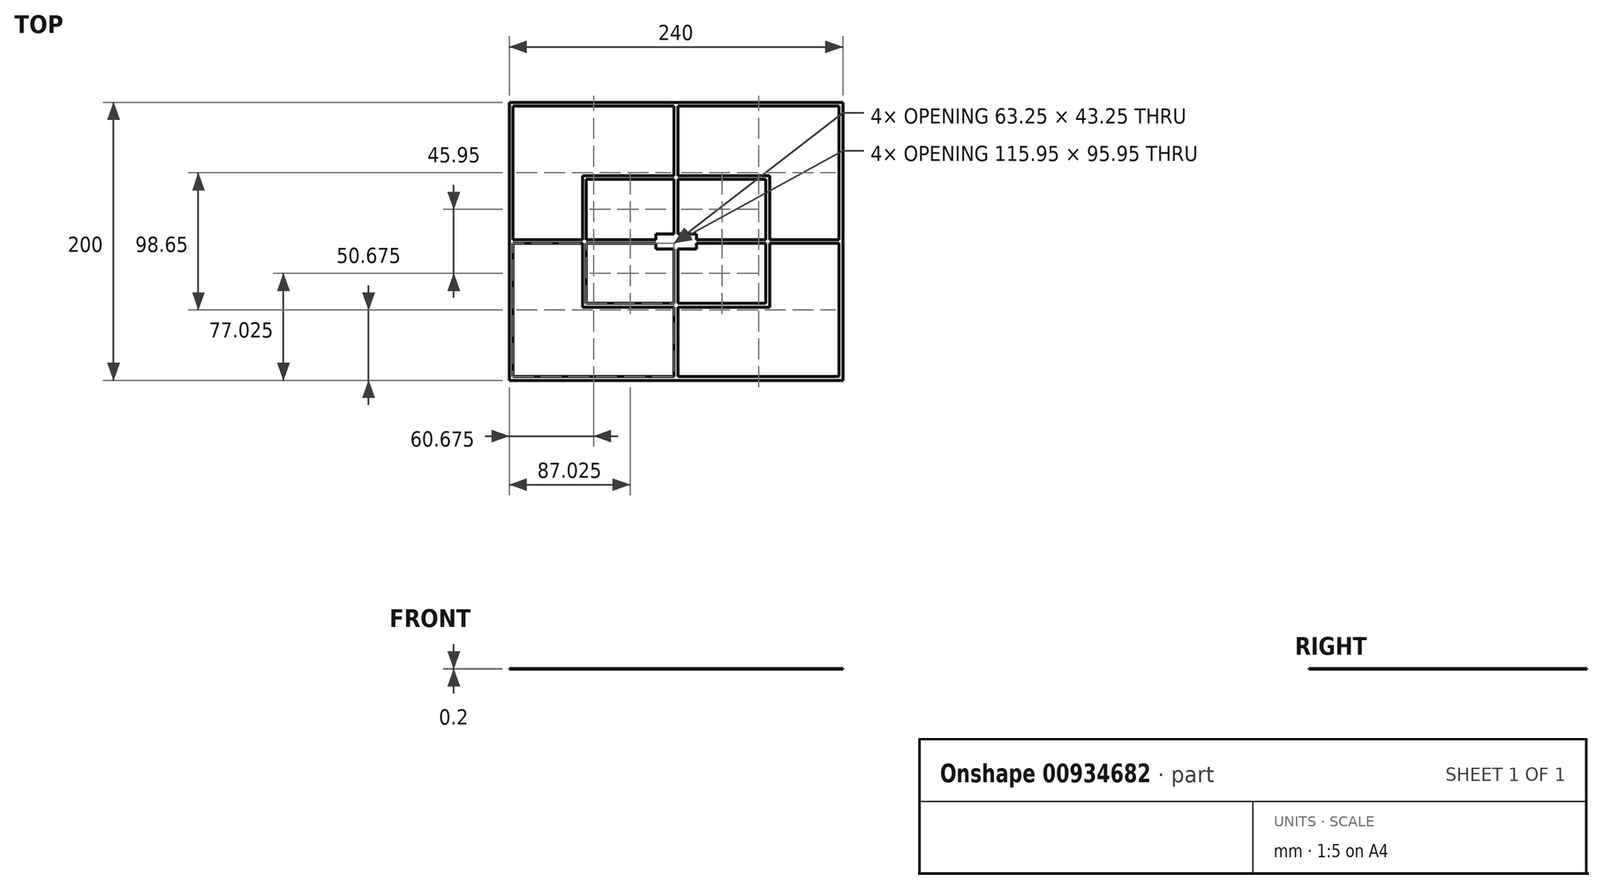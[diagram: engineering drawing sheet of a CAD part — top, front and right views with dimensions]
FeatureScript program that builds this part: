
annotation { "Feature Type Name" : "Feature", "Feature Type Description" : "" }
export const myFeature = defineFeature(function(context is Context, id is Id, definition is map)
    precondition{}
    {
        {
            assignVariable(context, id + "F0", {"variableType" : VariableType.LENGTH, "name" : "t", "lengthValue" : 0.2 * mm});
        }
        {
            var Q0;
            Q0=qCreatedBy(makeId("Top.planeOp"),FACE);
            var sketch = newSketch(context, id + "F1", { "sketchPlane" : qUnion([Q0])});
            skLineSegment(sketch, "E0.bottom", {"start": v(120, -100) * mm, "end": v(-120, -100) * mm});
            skLineSegment(sketch, "E0.top", {"start": v(120, 100) * mm, "end": v(-120, 100) * mm});
            skLineSegment(sketch, "E0.left", {"start": v(120, -100) * mm, "end": v(120, 100) * mm});
            skLineSegment(sketch, "E0.right", {"start": v(-120, -100) * mm, "end": v(-120, 100) * mm});
            skPoint(sketch, "E0.middle", {"position": v(0, 0) * mm});
            skLineSegment(sketch, "E1.0", {"start": v(117.3, -97.3) * mm, "end": v(117.3, -1.35) * mm});
            skLineSegment(sketch, "E1.1", {"start": v(117.3, -97.3) * mm, "end": v(1.35, -97.3) * mm});
            skLineSegment(sketch, "E1.2", {"start": v(-117.3, -97.3) * mm, "end": v(-117.3, -1.35) * mm});
            skLineSegment(sketch, "E1.3", {"start": v(117.3, 97.3) * mm, "end": v(1.35, 97.3) * mm});
            skLineSegment(sketch, "E2.0", {"start": v(-67.3, -47.3) * mm, "end": v(-67.3, -1.35) * mm});
            skLineSegment(sketch, "E2.1", {"start": v(67.3, -47.3) * mm, "end": v(1.35, -47.3) * mm});
            skLineSegment(sketch, "E2.2", {"start": v(67.3, -47.3) * mm, "end": v(67.3, -1.35) * mm});
            skLineSegment(sketch, "E2.3", {"start": v(67.3, 47.3) * mm, "end": v(1.35, 47.3) * mm});
            skLineSegment(sketch, "E3.0", {"start": v(64.6, -44.6) * mm, "end": v(1.35, -44.6) * mm});
            skLineSegment(sketch, "E3.1", {"start": v(64.6, -44.6) * mm, "end": v(64.6, -1.35) * mm});
            skLineSegment(sketch, "E3.2", {"start": v(64.6, 44.6) * mm, "end": v(1.35, 44.6) * mm});
            skLineSegment(sketch, "E3.3", {"start": v(-64.6, -44.6) * mm, "end": v(-64.6, -1.35) * mm});
            skLineSegment(sketch, "E4.0", {"start": v(14.6, 5.4) * mm, "end": v(1.35, 5.4) * mm});
            skLineSegment(sketch, "E4.1", {"start": v(14.6, 1.35) * mm, "end": v(14.6, 5.4) * mm});
            skLineSegment(sketch, "E4.2", {"start": v(14.6, -5.4) * mm, "end": v(1.35, -5.4) * mm});
            skLineSegment(sketch, "E4.3", {"start": v(-14.6, 1.35) * mm, "end": v(-14.6, 5.4) * mm});
            skLineSegment(sketch, "E5", {"start": v(14.6, -1.35) * mm, "end": v(64.6, -1.35) * mm});
            skLineSegment(sketch, "E6", {"start": v(67.3, -1.35) * mm, "end": v(117.3, -1.35) * mm});
            skLineSegment(sketch, "E7.MirrorCS", {"start": v(14.6, 1.35) * mm, "end": v(64.6, 1.35) * mm});
            skLineSegment(sketch, "E8.MirrorCS", {"start": v(67.3, 1.35) * mm, "end": v(117.3, 1.35) * mm});
            skPoint(sketch, "E9.orphan", {"position": v(64.6, 1.35) * mm});
            skLineSegment(sketch, "E10.trimOffspring", {"start": v(67.3, 1.35) * mm, "end": v(67.3, 47.3) * mm});
            skLineSegment(sketch, "E11.trimOffspring", {"start": v(64.6, 1.35) * mm, "end": v(64.6, 44.6) * mm});
            skLineSegment(sketch, "E12.trimOffspring", {"start": v(117.3, 1.35) * mm, "end": v(117.3, 97.3) * mm});
            skLineSegment(sketch, "E13.trimOffspring", {"start": v(14.6, -5.4) * mm, "end": v(14.6, -1.35) * mm});
            skLineSegment(sketch, "E14", {"start": v(1.35, 5.4) * mm, "end": v(1.35, 44.6) * mm});
            skLineSegment(sketch, "E15.MirrorCS", {"start": v(-1.35, 5.4) * mm, "end": v(-1.35, 44.6) * mm});
            skLineSegment(sketch, "E16.trimOffspring", {"start": v(-1.35, 97.3) * mm, "end": v(-117.3, 97.3) * mm});
            skPoint(sketch, "E17.orphan", {"position": v(1.35, 100) * mm});
            skPoint(sketch, "E18.orphan", {"position": v(-1.35, 100) * mm});
            skLineSegment(sketch, "E19.trimOffspring", {"start": v(-1.35, 44.6) * mm, "end": v(-64.6, 44.6) * mm});
            skLineSegment(sketch, "E20.trimOffspring", {"start": v(-1.35, 47.3) * mm, "end": v(-67.3, 47.3) * mm});
            skLineSegment(sketch, "E21.trimOffspring", {"start": v(-1.35, 47.3) * mm, "end": v(-1.35, 97.3) * mm});
            skLineSegment(sketch, "E22.trimOffspring", {"start": v(1.35, 47.3) * mm, "end": v(1.35, 97.3) * mm});
            skLineSegment(sketch, "E23.trimOffspring", {"start": v(-1.35, 5.4) * mm, "end": v(-14.6, 5.4) * mm});
            skLineSegment(sketch, "E24.MirrorCS", {"start": v(1.35, -5.4) * mm, "end": v(1.35, -44.6) * mm});
            skLineSegment(sketch, "E25.MirrorCS", {"start": v(-1.35, -5.4) * mm, "end": v(-1.35, -44.6) * mm});
            skLineSegment(sketch, "E26.MirrorCS", {"start": v(1.35, -47.3) * mm, "end": v(1.35, -97.3) * mm});
            skLineSegment(sketch, "E27.MirrorCS", {"start": v(-1.35, -47.3) * mm, "end": v(-1.35, -97.3) * mm});
            skLineSegment(sketch, "E28.MirrorCS", {"start": v(-67.3, -1.35) * mm, "end": v(-117.3, -1.35) * mm});
            skLineSegment(sketch, "E29.MirrorCS", {"start": v(-67.3, 1.35) * mm, "end": v(-117.3, 1.35) * mm});
            skLineSegment(sketch, "E30.MirrorCS", {"start": v(-14.6, 1.35) * mm, "end": v(-64.6, 1.35) * mm});
            skLineSegment(sketch, "E31.MirrorCS", {"start": v(-14.6, -1.35) * mm, "end": v(-64.6, -1.35) * mm});
            skLineSegment(sketch, "E32.trimOffspring", {"start": v(-1.35, -97.3) * mm, "end": v(-117.3, -97.3) * mm});
            skLineSegment(sketch, "E33.trimOffspring", {"start": v(-1.35, -47.3) * mm, "end": v(-67.3, -47.3) * mm});
            skLineSegment(sketch, "E34.trimOffspring", {"start": v(-1.35, -44.6) * mm, "end": v(-64.6, -44.6) * mm});
            skLineSegment(sketch, "E35.trimOffspring", {"start": v(-1.35, -5.4) * mm, "end": v(-14.6, -5.4) * mm});
            skLineSegment(sketch, "E36.trimOffspring", {"start": v(-14.6, -5.4) * mm, "end": v(-14.6, -1.35) * mm});
            skLineSegment(sketch, "E37.trimOffspring", {"start": v(-64.6, 1.35) * mm, "end": v(-64.6, 44.6) * mm});
            skLineSegment(sketch, "E38.trimOffspring", {"start": v(-67.3, 1.35) * mm, "end": v(-67.3, 47.3) * mm});
            skLineSegment(sketch, "E39.trimOffspring", {"start": v(-117.3, 1.35) * mm, "end": v(-117.3, 97.3) * mm});
            skSolve(sketch);
        }
        {
            var Q0;
            Q0 = qSketchRegion(id + "F1", true);
            var Q1;
            Q1=makeQuery(id+"F1.imprint","IMPRINT",FACE,{"disambiguationData":[TD([[makeQuery(id+"F1.imprint","IMPRINT",EDGE,{"derivedFrom":sQuery(id+"F1.wireOp",EDGE,"E2.0")}),-1.0]])]});
            var Q2;
            Q2=makeQuery(id+"F1.imprint","IMPRINT",FACE,{"disambiguationData":[TD([[makeQuery(id+"F1.imprint","IMPRINT",EDGE,{"derivedFrom":sQuery(id+"F1.wireOp",EDGE,"E4.0")}),1.0]])]});
            extrude(context, id + "F2", {"entities" : qUnion([Q0, Q1, Q2]), "depth" : getVariable(context, 't'), "offsetDistance" : 25 * mm});
        }
    });
